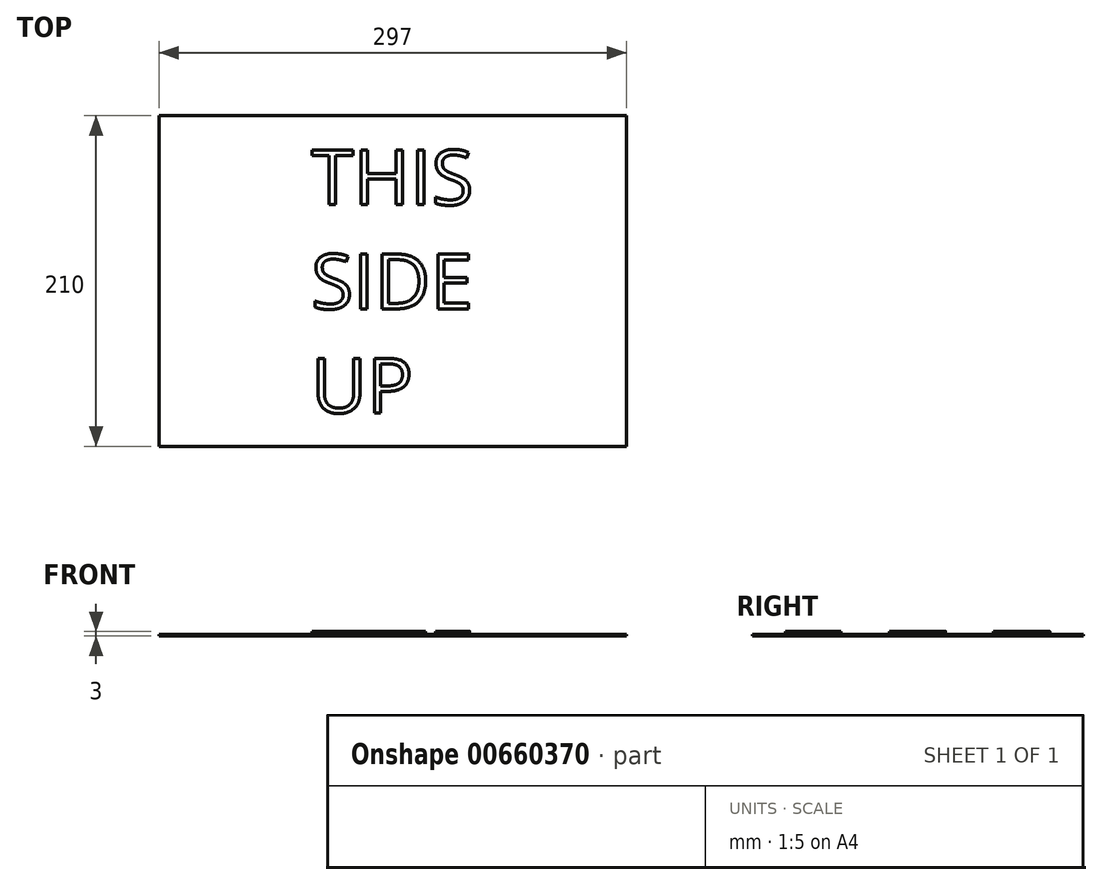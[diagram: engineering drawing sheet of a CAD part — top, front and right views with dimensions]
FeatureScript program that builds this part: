
annotation { "Feature Type Name" : "Feature", "Feature Type Description" : "" }
export const myFeature = defineFeature(function(context is Context, id is Id, definition is map)
    precondition{}
    {
        {
            var Q0;
            Q0=qCreatedBy(makeId("Top.planeOp"),FACE);
            var sketch = newSketch(context, id + "F0", { "sketchPlane" : qUnion([Q0])});
            skLineSegment(sketch, "E0.bottom", {"start": v(-251.93, 163.61) * mm, "end": v(45.07, 163.61) * mm});
            skLineSegment(sketch, "E0.top", {"start": v(-251.93, -46.39) * mm, "end": v(45.07, -46.39) * mm});
            skLineSegment(sketch, "E0.left", {"start": v(-251.93, 163.61) * mm, "end": v(-251.93, -46.39) * mm});
            skLineSegment(sketch, "E0.right", {"start": v(45.07, 163.61) * mm, "end": v(45.07, -46.39) * mm});
            skSolve(sketch);
        }
        {
            var Q0;
            Q0=makeQuery(id+"F0.imprint","IMPRINT",FACE,{"disambiguationData":[TD([[makeQuery(id+"F0.imprint","IMPRINT",EDGE,{"derivedFrom":sQuery(id+"F0.wireOp",EDGE,"E0.bottom")}),-1.0]])]});
            extrude(context, id + "F1", {"entities" : qUnion([Q0]), "depth" : 1 * mm, "offsetDistance" : 25 * mm});
        }
        {
            var Q0;
            Q0=makeQuery(id+"F1.opExtrude","CAP_FACE",FACE,{"disambiguationData":[OSD([sQuery(id+"F0.wireOp",EDGE,"E0.bottom"),sQuery(id+"F0.wireOp",EDGE,"E0.top"),sQuery(id+"F0.wireOp",EDGE,"E0.left"),sQuery(id+"F0.wireOp",EDGE,"E0.right")])],"isStart":false});
            var sketch = newSketch(context, id + "F2", { "sketchPlane" : qUnion([Q0])});
            skText(sketch, "E1", { "text": "THIS\nSIDE\nUP", "fontName": "OpenSans-Regular.ttf"});
            const initialGuessF2  = {"E1": [-0.15533, 0.1071, 1, 0, 0.035]};
            skSetInitialGuess(sketch, initialGuessF2);
            skSolve(sketch);
        }
        {
            var Q0;
            Q0=qSketchRegion(id+"F2",true);
            extrude(context, id + "F3", {"entities" : qUnion([Q0]), "operationType" : NewBodyOperationType.ADD, "depth" : 2 * mm, "offsetDistance" : 25 * mm});
        }
    });
